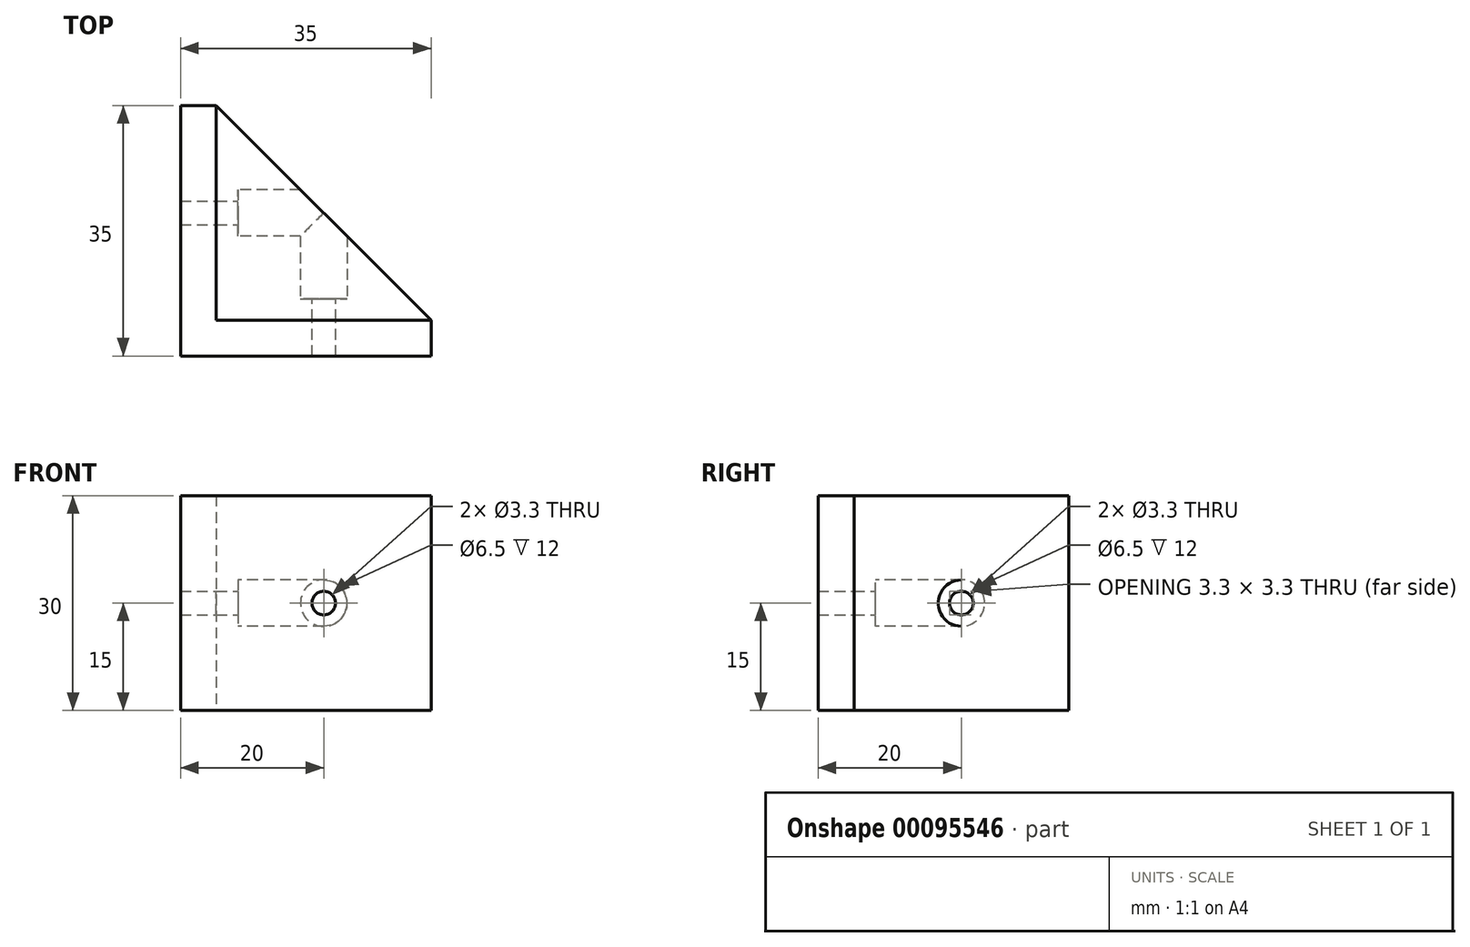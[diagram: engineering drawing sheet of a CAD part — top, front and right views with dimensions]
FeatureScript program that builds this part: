
annotation { "Feature Type Name" : "Feature", "Feature Type Description" : "" }
export const myFeature = defineFeature(function(context is Context, id is Id, definition is map)
    precondition{}
    {
        {
            assignVariable(context, id + "F0", {"name" : "c", "anyValue" : 30});
        }
        {
            var Q0;
            Q0=qCreatedBy(makeId("Top.planeOp"),FACE);
            var sketch = newSketch(context, id + "F1", { "sketchPlane" : qUnion([Q0])});
            skLineSegment(sketch, "E0.top", {"start": v(15, -15) * mm, "end": v(-15, -15) * mm});
            skLineSegment(sketch, "E0.right", {"start": v(-15, 15) * mm, "end": v(-15, -15) * mm});
            skPoint(sketch, "E0.middle", {"position": v(0, 0) * mm});
            skLineSegment(sketch, "E1", {"start": v(-15, 15) * mm, "end": v(15, -15) * mm});
            skSolve(sketch);
        }
        {
            var Q0;
            Q0=qSketchRegion(id+"F1",true);
            extrude(context, id + "F2", {"entities" : qUnion([Q0]), "depth" : (getVariable(context, 'c')) * mm});
        }
        {
            var Q0;
            Q0=makeQuery(id+"F2.opExtrude","SWEPT_FACE",FACE,{"disambiguationData":[OSD([sQuery(id+"F1.wireOp",EDGE,"E0.right")])]});
            cPlane(context, id + "F3", {"entities" : qUnion([Q0]), "cplaneType" : CPlaneType.OFFSET, "offset" : 3 * mm, "oppositeDirection" : true, "width" : 150 * mm, "height" : 150 * mm});
        }
        {
            var Q0;
            Q0=qCreatedBy(id+"F3.planeOp",FACE);
            var sketch = newSketch(context, id + "F4", { "sketchPlane" : qUnion([Q0])});
            skCircle(sketch, "E2", {"center": v(0, 15) * mm, "radius": 3.25 * mm});
            skPoint(sketch, "E3", {"position": v(15, 15) * mm});
            skSolve(sketch);
        }
        {
            var Q0;
            Q0=qSketchRegion(id+"F4",true);
            extrude(context, id + "F5", {"entities" : qUnion([Q0]), "operationType" : NewBodyOperationType.REMOVE, "endBound" : BoundingType.THROUGH_ALL, "oppositeDirection" : true, "depth" : 25 * mm});
        }
        {
            var Q0;
            Q0=qCreatedBy(id+"F3.planeOp",FACE);
            var sketch = newSketch(context, id + "F6", { "sketchPlane" : qUnion([Q0])});
            skPoint(sketch, "E4.0", {"position": v(0, 15) * mm});
            skCircle(sketch, "E5", {"center": v(0, 15) * mm, "radius": 1.65 * mm});
            skSolve(sketch);
        }
        {
            var Q0;
            Q0=qSketchRegion(id+"F6",true);
            extrude(context, id + "F7", {"entities" : qUnion([Q0]), "operationType" : NewBodyOperationType.REMOVE, "endBound" : BoundingType.THROUGH_ALL, "depth" : 25 * mm});
        }
        {
            var Q0;
            Q0=makeQuery(id+"F2.opExtrude","SWEPT_FACE",FACE,{"disambiguationData":[OSD([sQuery(id+"F1.wireOp",EDGE,"E0.top")])]});
            cPlane(context, id + "F8", {"entities" : qUnion([Q0]), "cplaneType" : CPlaneType.OFFSET, "offset" : 3 * mm, "oppositeDirection" : true, "width" : 150 * mm, "height" : 150 * mm});
        }
        {
            var Q0;
            Q0=qCreatedBy(id+"F8.planeOp",FACE);
            var sketch = newSketch(context, id + "F9", { "sketchPlane" : qUnion([Q0])});
            skCircle(sketch, "E6", {"center": v(0, 15) * mm, "radius": 3.25 * mm});
            skPoint(sketch, "E7", {"position": v(15, 15) * mm});
            skSolve(sketch);
        }
        {
            var Q0;
            Q0=qSketchRegion(id+"F9",true);
            extrude(context, id + "F10", {"entities" : qUnion([Q0]), "operationType" : NewBodyOperationType.REMOVE, "endBound" : BoundingType.THROUGH_ALL, "oppositeDirection" : true, "depth" : 25 * mm});
        }
        {
            var Q0;
            Q0=qCreatedBy(id+"F8.planeOp",FACE);
            var sketch = newSketch(context, id + "F11", { "sketchPlane" : qUnion([Q0])});
            skPoint(sketch, "E8.0", {"position": v(0, 15) * mm});
            skCircle(sketch, "E9", {"center": v(0, 15) * mm, "radius": 1.65 * mm});
            skSolve(sketch);
        }
        {
            var Q0;
            Q0=qSketchRegion(id+"F11",true);
            extrude(context, id + "F12", {"entities" : qUnion([Q0]), "operationType" : NewBodyOperationType.REMOVE, "depth" : 25 * mm});
        }
        {
            var Q0;
            Q0=makeQuery(id+"F2.opExtrude","SWEPT_FACE",FACE,{"disambiguationData":[OSD([sQuery(id+"F1.wireOp",EDGE,"E0.top")])]});
            extrude(context, id + "F13", {"entities" : qUnion([Q0]), "depth" : 2.5 * mm});
        }
        {
            var Q0;
            Q0=makeQuery(id+"F2.opExtrude","SWEPT_FACE",FACE,{"disambiguationData":[OSD([sQuery(id+"F1.wireOp",EDGE,"E0.right")])]});
            var sketch = newSketch(context, id + "F14", { "sketchPlane" : qUnion([Q0])});
            skLineSegment(sketch, "E10.bottom", {"start": v(-15, 30) * mm, "end": v(17.5, 30) * mm});
            skLineSegment(sketch, "E10.top", {"start": v(-15, 0) * mm, "end": v(17.5, 0) * mm});
            skLineSegment(sketch, "E10.left", {"start": v(-15, 30) * mm, "end": v(-15, 0) * mm});
            skLineSegment(sketch, "E10.right", {"start": v(17.5, 30) * mm, "end": v(17.5, 0) * mm});
            skSolve(sketch);
        }
        {
            var Q0;
            Q0 = qSketchRegion(id + "F14", true);
            extrude(context, id + "F15", {"entities" : qUnion([Q0]), "depth" : 2.5 * mm});
        }
        {
            var Q0;
            Q0=makeQuery(id+"F15.opExtrude","CAP_FACE",FACE,{"disambiguationData":[OSD([sQuery(id+"F14.wireOp",EDGE,"E10.bottom"),sQuery(id+"F14.wireOp",EDGE,"E10.top"),sQuery(id+"F14.wireOp",EDGE,"E10.left"),sQuery(id+"F14.wireOp",EDGE,"E10.right")])],"isStart":false});
            extrude(context, id + "F16", {"entities" : qUnion([Q0]), "depth" : 2.5 * mm});
        }
        {
            var Q0;
            Q0=makeQuery(id+"F13.opExtrude","CAP_FACE",FACE,{"disambiguationData":[OSD([sQuery(id+"F1.wireOp",EDGE,"E0.top")])],"isStart":false});
            var sketch = newSketch(context, id + "F17", { "sketchPlane" : qUnion([Q0])});
            skLineSegment(sketch, "E11.bottom", {"start": v(15, 0) * mm, "end": v(-20, 0) * mm});
            skLineSegment(sketch, "E11.top", {"start": v(15, 30) * mm, "end": v(-20, 30) * mm});
            skLineSegment(sketch, "E11.left", {"start": v(15, 0) * mm, "end": v(15, 30) * mm});
            skLineSegment(sketch, "E11.right", {"start": v(-20, 0) * mm, "end": v(-20, 30) * mm});
            skSolve(sketch);
        }
        {
            var Q0;
            Q0 = qSketchRegion(id + "F17", true);
            extrude(context, id + "F18", {"entities" : qUnion([Q0]), "operationType" : NewBodyOperationType.ADD, "depth" : 2.5 * mm});
        }
        {
            var Q0;
            Q0=makeQuery(id+"F9.imprint","IMPRINT",FACE,{"disambiguationData":[TD([[makeQuery(id+"F9.imprint","IMPRINT",EDGE,{"derivedFrom":sQuery(id+"F9.wireOp",EDGE,"E6")}),1.0]])]});
            var sketch = newSketch(context, id + "F19", { "sketchPlane" : qUnion([Q0])});
            skCircle(sketch, "E12", {"center": v(0, 15) * mm, "radius": 1.65 * mm});
            skSolve(sketch);
        }
        {
            var Q0;
            Q0 = qSketchRegion(id + "F19", true);
            extrude(context, id + "F20", {"entities" : qUnion([Q0]), "operationType" : NewBodyOperationType.REMOVE, "depth" : 25 * mm});
        }
        {
            var Q0;
            Q0=makeQuery(id+"F15.opExtrude","CAP_FACE",FACE,{"disambiguationData":[OSD([sQuery(id+"F14.wireOp",EDGE,"E10.bottom"),sQuery(id+"F14.wireOp",EDGE,"E10.top"),sQuery(id+"F14.wireOp",EDGE,"E10.left"),sQuery(id+"F14.wireOp",EDGE,"E10.right")])],"isStart":true});
            var sketch = newSketch(context, id + "F21", { "sketchPlane" : qUnion([Q0])});
            skCircle(sketch, "E13", {"center": v(0, 15) * mm, "radius": 1.65 * mm});
            skSolve(sketch);
        }
        {
            var Q0;
            Q0 = qSketchRegion(id + "F21", true);
            extrude(context, id + "F22", {"entities" : qUnion([Q0]), "operationType" : NewBodyOperationType.REMOVE, "oppositeDirection" : true, "depth" : 25 * mm});
        }
    });
